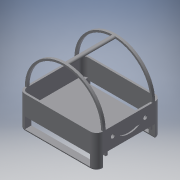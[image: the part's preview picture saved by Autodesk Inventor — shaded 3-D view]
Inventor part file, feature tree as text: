
AUTODESK INVENTOR PART (.ipt)
format: ipt  version: 2019 (Build 230136000, 136)  size: 331,264 bytes
history: native  units: in
note: dims shown in document units (in); Inventor stores cm internally (conversion verified against a paired STEP export)
features: sketch x11, extrude x8, plane x3, sweep x2, fillet x2, shell x1, revolve x1
ambient origin geometry x8: Origin, YZ Plane, XZ Plane, XY Plane, X Axis, Y Axis, Z Axis, Center Point
bodies: Solid1 (feature_tree)
feature tree (28):
  extrude  "Extrusion1"  Depth=6.0in
  shell  "Shell1"  Thickness=0.5in
  plane  "Work Plane1"
  sweep  "Sweep1"
  plane  "Work Plane2"
  sketch  "Sketch7"  dims[d11=90.0deg d12=0.35in d13=0.15in]
  revolve  "Revolution1"  [1 undecoded]
  plane  "Work Plane3"
  sweep  "Sweep2"
  fillet  "Fillet1"  Radius=0.15in
  extrude  "Extrusion2"  TaperAngle=0.0deg  [1 undecoded]
  sketch  "Sketch13"  dims[d22=0.75in d23=0.25in d24=0.0in]
  extrude  "Extrusion3"  Depth=0.125in TaperAngle=0.0deg
  extrude  "Extrusion4"  Depth=0.75in
  extrude  "Extrusion5"  Depth=0.25in TaperAngle=0.0deg
  extrude  "Extrusion6"  Depth=0.1in TaperAngle=0.0deg
  extrude  "Extrusion7"  Depth=0.15in TaperAngle=0.0deg
  fillet  "Fillet2"  Radius=0.125in
  extrude  "Extrusion8"  Depth=0.15in
  sketch  "Sketch1"  dims[d0=6.0in d1=5.0in d2=0.5in]
  sketch  "Sketch2"  dims[d3=1.5in d4=0.0in d5=0.15in]
  sketch  "Sketch4"  dims[d6=0.2in d7=0.0in d8=0.0in]
  sketch  "Sketch10"  dims[d14=0.175in d15=0.0in d16=0.0in]
  sketch  "Sketch11"  dims[d17=0.125in d18=0.4in d19=0.0in]
  sketch  "Sketch12"  dims[d20=0.3in d21=0.75in]
  sketch  "Sketch14"  dims[d25=0.05in d26=0.0in d27=0.1in d28=0.0in]
  sketch  "Sketch15"  dims[d29=1.0in d30=0.0in d31=0.15in d32=0.0in d33=0.125in]
  sketch  "Sketch16"  dims[d36=6.0in d37=0.15in d38=0.15in d39=0.2in d40=0.2in d41=0.25in d42=0.0in]
note: 2 required parameter values undecoded (feature->parameter linkage not recoverable at this tier; creation-order binding heuristic only, values carry confidence <= 0.55)